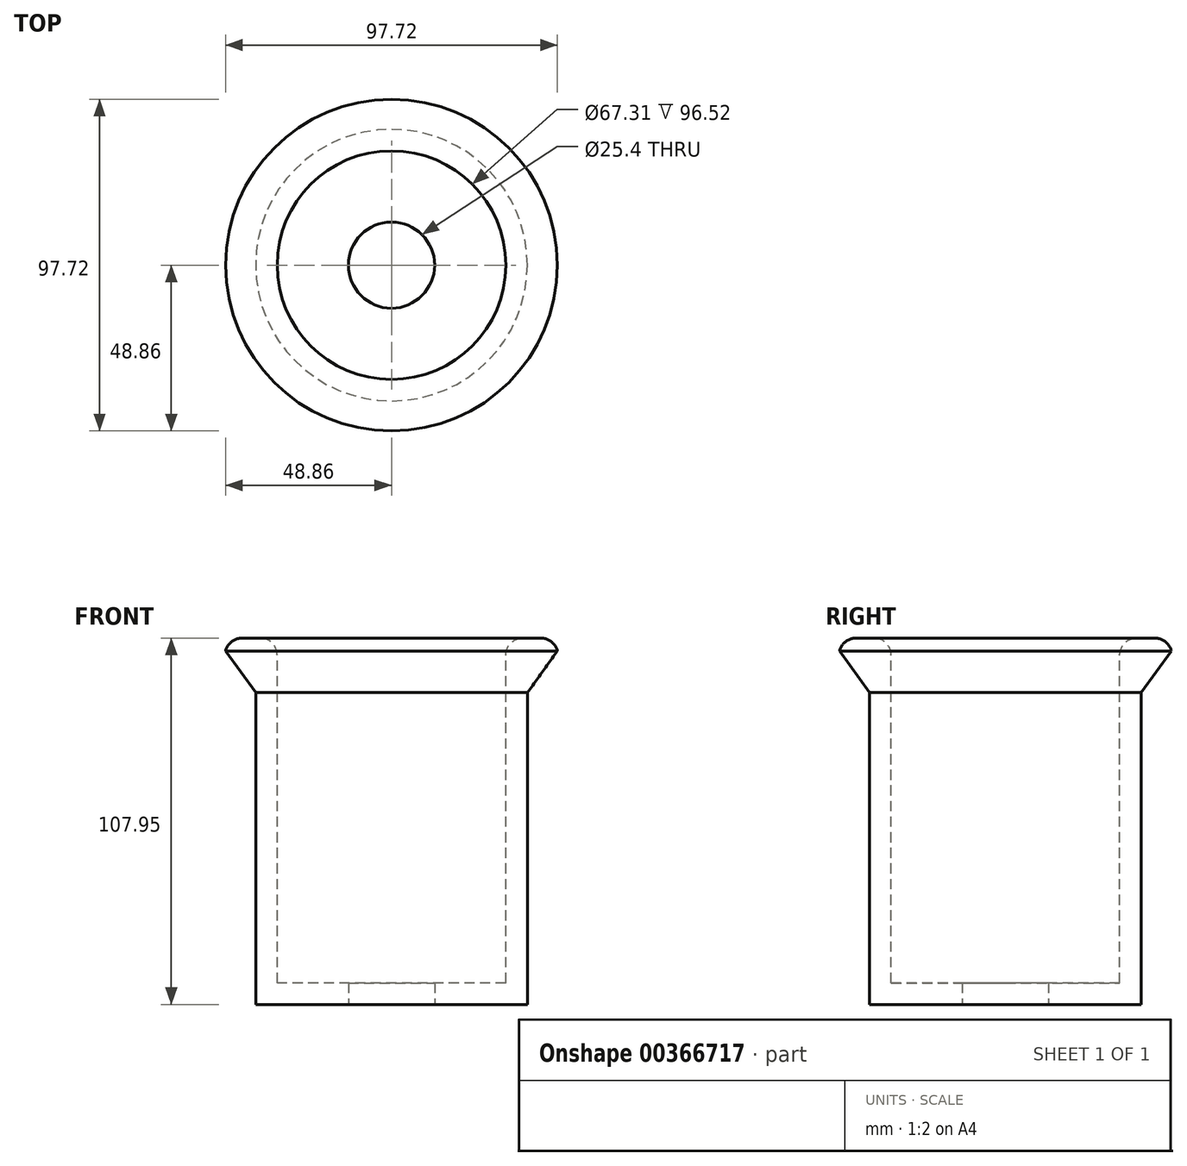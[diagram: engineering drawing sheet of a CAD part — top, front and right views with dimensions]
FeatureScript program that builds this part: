
annotation { "Feature Type Name" : "Feature", "Feature Type Description" : "" }
export const myFeature = defineFeature(function(context is Context, id is Id, definition is map)
    precondition{}
    {
        {
            var Q0;
            Q0=qCreatedBy(makeId("Front.planeOp"),FACE);
            var sketch = newSketch(context, id + "F0", { "sketchPlane" : qUnion([Q0])});
            skLineSegment(sketch, "E0", {"start": v(-40, 107.95) * mm, "end": v(-33.66, 107.95) * mm});
            skLineSegment(sketch, "E1", {"start": v(-33.65, 6.35) * mm, "end": v(0, 6.35) * mm});
            skLineSegment(sketch, "E2", {"start": v(0, 6.35) * mm, "end": v(0, 0) * mm});
            skLineSegment(sketch, "E3", {"start": v(0, 0) * mm, "end": v(-40, 0) * mm});
            skLineSegment(sketch, "E4", {"start": v(-40, 0) * mm, "end": v(-40, 91.85) * mm});
            skLineSegment(sketch, "E5", {"start": v(-33.66, 107.95) * mm, "end": v(-33.66, 6.35) * mm});
            skLineSegment(sketch, "E6", {"start": v(-40, 107.95) * mm, "end": v(-48.86, 107.95) * mm});
            skLineSegment(sketch, "E7", {"start": v(-48.86, 107.95) * mm, "end": v(-48.86, 104.11) * mm});
            skLineSegment(sketch, "E8", {"start": v(-48.86, 104.11) * mm, "end": v(-40, 91.85) * mm});
            skSolve(sketch);
        }
        {
            var Q0;
            Q0=makeQuery(id+"F0.imprint","IMPRINT",FACE,{"disambiguationData":[TD([[makeQuery(id+"F0.imprint","IMPRINT",EDGE,{"derivedFrom":sQuery(id+"F0.wireOp",EDGE,"E0")}),-1.0]])]});
            var Q1;
            Q1=sQuery(id+"F0.wireOp",EDGE,"E2");
            revolve(context, id + "F1", {"entities" : qUnion([Q0]), "axis" : qUnion([Q1]), "revolveType" : RevolveType.FULL});
        }
        {
            var Q0;
            Q0=makeQuery(id+"F1.opRevolve","SWEPT_EDGE",EDGE,{"disambiguationData":[OSD([sQuery(id+"F0.wireOp",EDGE,"E0"),sQuery(id+"F0.wireOp",EDGE,"E5")])]});
            var Q1;
            Q1=makeQuery(id+"F1.opRevolve","SWEPT_EDGE",EDGE,{"disambiguationData":[OSD([sQuery(id+"F0.wireOp",EDGE,"E6"),sQuery(id+"F0.wireOp",EDGE,"E7")])]});
            fillet(context, id + "F2", {"entities" : qUnion([Q0, Q1]), "radius" : 5.08 * mm, "tangentPropagation" : true, "allowEdgeOverflow" : false});
        }
        {
            var Q0;
            Q0=qCreatedBy(makeId("Top.planeOp"),FACE);
            var sketch = newSketch(context, id + "F3", { "sketchPlane" : qUnion([Q0])});
            skCircle(sketch, "E9", {"center": v(0, 0) * mm, "radius": 12.53 * mm});
            skSolve(sketch);
        }
        {
            var Q0;
            Q0=sQuery(id+"F3.wireOp",VERTEX,"E9.center");
            var Q1;
            Q1=makeQuery(id+"F1.opRevolve","SWEPT_BODY",BODY,{"disambiguationData":[OSD([sQuery(id+"F0.wireOp",EDGE,"E0"),sQuery(id+"F0.wireOp",EDGE,"E1"),sQuery(id+"F0.wireOp",EDGE,"E2"),sQuery(id+"F0.wireOp",EDGE,"E3"),sQuery(id+"F0.wireOp",EDGE,"E4"),sQuery(id+"F0.wireOp",EDGE,"E5"),sQuery(id+"F0.wireOp",EDGE,"E6"),sQuery(id+"F0.wireOp",EDGE,"E7"),sQuery(id+"F0.wireOp",EDGE,"E8")])]});
            hole(context, id + "F4", {"style" : HoleStyle.SIMPLE, "endStyle" : HoleEndStyle.THROUGH, "oppositeDirection" : true, "holeDiameter" : 25.4 * mm, "isTappedThrough" : true, "tappedDepth" : 12.7 * mm, "tapClearance" : 3, "startFromSketch" : true, "locations" : qUnion([Q0]), "scope" : qUnion([Q1])});
        }
    });
